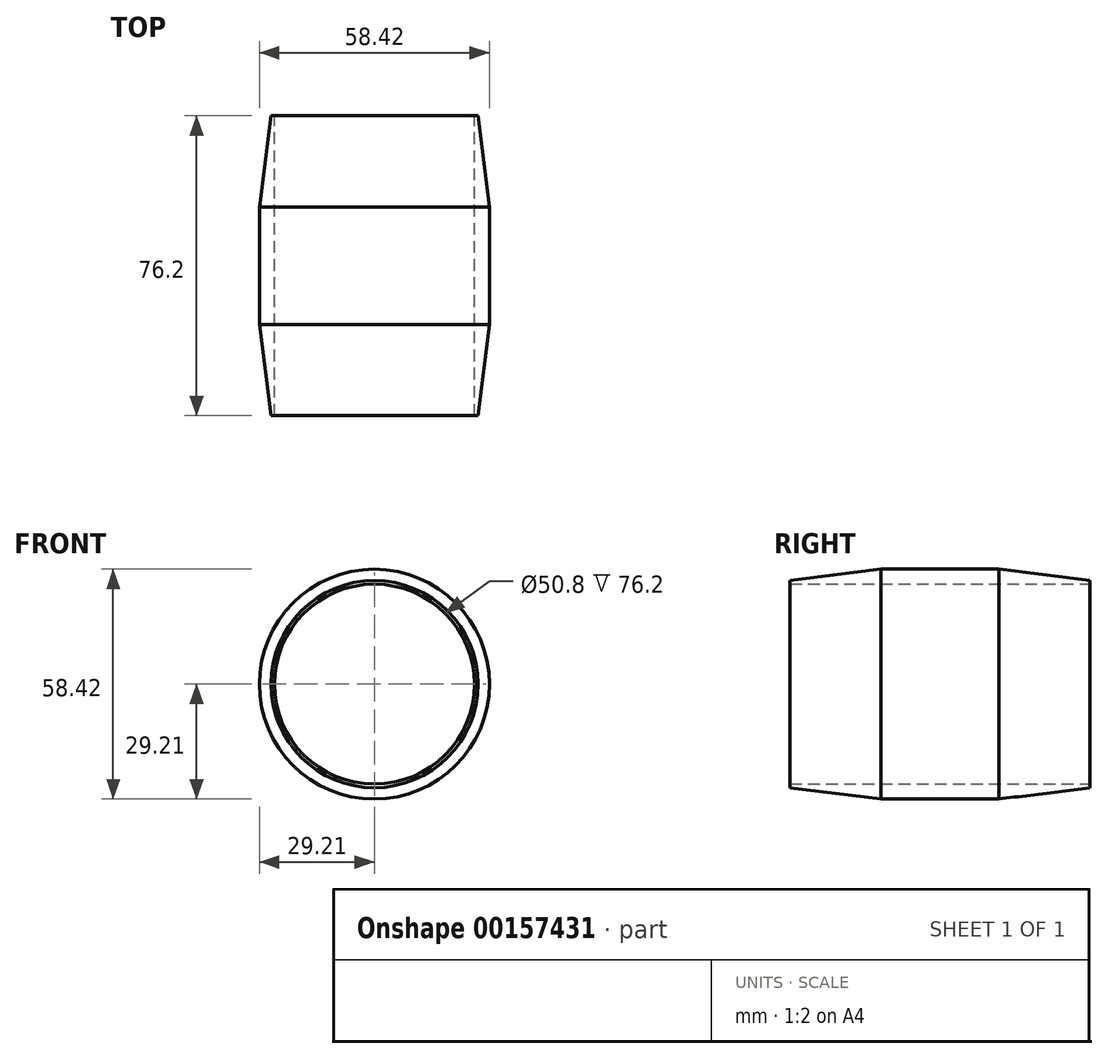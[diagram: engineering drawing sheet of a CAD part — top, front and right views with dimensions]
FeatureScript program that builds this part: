
annotation { "Feature Type Name" : "Feature", "Feature Type Description" : "" }
export const myFeature = defineFeature(function(context is Context, id is Id, definition is map)
    precondition{}
    {
        {
            var Q0;
            Q0=qCreatedBy(makeId("Front.planeOp"),FACE);
            var sketch = newSketch(context, id + "F0", { "sketchPlane" : qUnion([Q0])});
            skCircle(sketch, "E0", {"center": v(0, 0) * mm, "radius": 29.21 * mm});
            skCircle(sketch, "E1", {"center": v(0, 0) * mm, "radius": 25.4 * mm});
            skSolve(sketch);
        }
        {
            var Q0;
            Q0 = qSketchRegion(id + "F0", true);
            extrude(context, id + "F1", {"entities" : qUnion([Q0]), "depth" : 76.2 * mm});
        }
        {
            var Q0;
            Q0=qCreatedBy(makeId("Right.planeOp"),FACE);
            var sketch = newSketch(context, id + "F2", { "sketchPlane" : qUnion([Q0])});
            skLineSegment(sketch, "E2", {"start": v(0, 29.49) * mm, "end": v(-25.4, 29.49) * mm});
            skLineSegment(sketch, "E3", {"start": v(-25.4, 29.49) * mm, "end": v(0, 26.31) * mm});
            skLineSegment(sketch, "E4", {"start": v(0, 26.31) * mm, "end": v(0, 29.49) * mm});
            skLineSegment(sketch, "E5", {"start": v(-76.23, 29.49) * mm, "end": v(-50.83, 29.49) * mm});
            skLineSegment(sketch, "E6", {"start": v(-50.83, 29.49) * mm, "end": v(-76.23, 26.31) * mm});
            skLineSegment(sketch, "E7", {"start": v(-76.23, 26.31) * mm, "end": v(-76.23, 29.49) * mm});
            skLineSegment(sketch, "E8", {"start": v(-13.02, 0) * mm, "end": v(-64.09, 0) * mm});
            skSolve(sketch);
        }
        {
            var Q0;
            Q0 = qSketchRegion(id + "F2", true);
            var Q1;
            Q1=sQuery(id+"F2.wireOp",EDGE,"E8");
            revolve(context, id + "F3", {"operationType" : NewBodyOperationType.REMOVE, "entities" : qUnion([Q0]), "axis" : qUnion([Q1]), "revolveType" : RevolveType.FULL, "oppositeDirection" : true});
        }
    });
